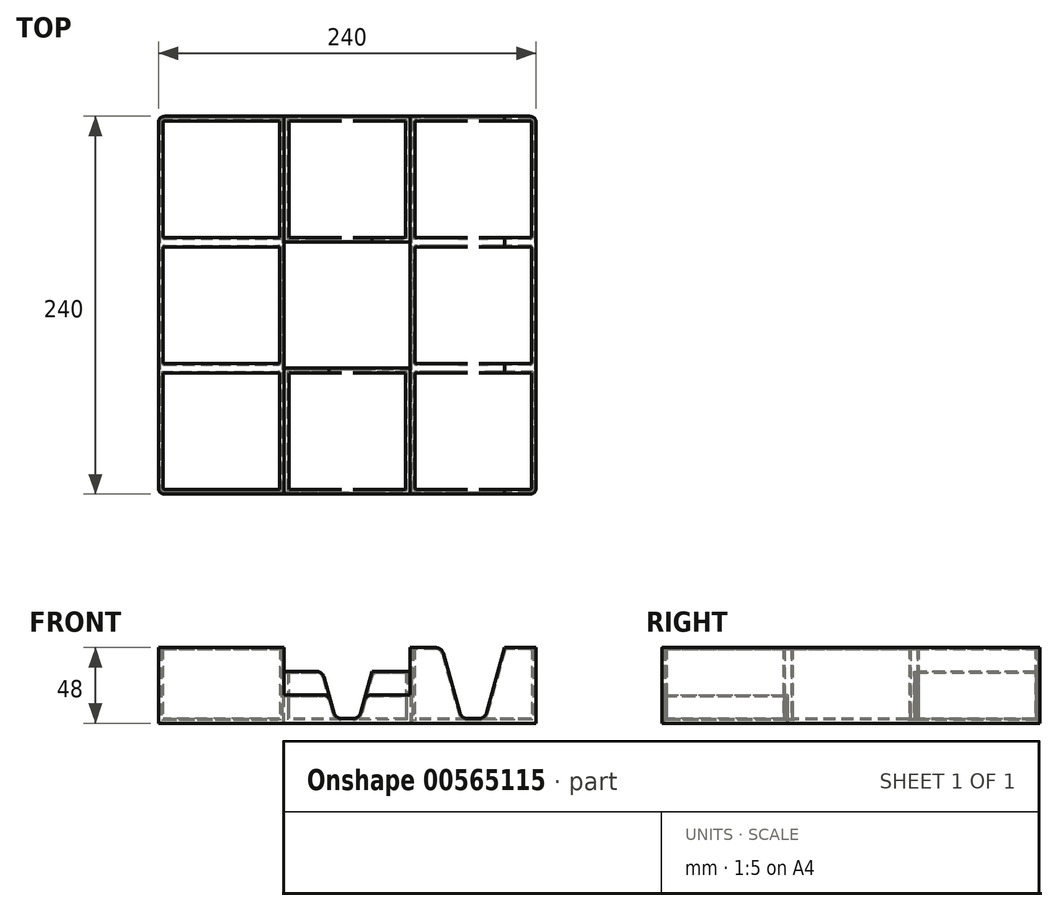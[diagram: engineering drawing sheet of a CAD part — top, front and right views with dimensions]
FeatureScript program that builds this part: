
annotation { "Feature Type Name" : "Feature", "Feature Type Description" : "" }
export const myFeature = defineFeature(function(context is Context, id is Id, definition is map)
    precondition{}
    {
        {
            var Q0;
            Q0=qCreatedBy(makeId("Top.planeOp"),FACE);
            var sketch = newSketch(context, id + "F0", { "sketchPlane" : qUnion([Q0])});
            skLineSegment(sketch, "E0.bottom", {"start": v(120, 120) * mm, "end": v(-120, 120) * mm});
            skLineSegment(sketch, "E0.top", {"start": v(120, -120) * mm, "end": v(-120, -120) * mm});
            skLineSegment(sketch, "E0.left", {"start": v(120, 120) * mm, "end": v(120, -120) * mm});
            skLineSegment(sketch, "E0.right", {"start": v(-120, 120) * mm, "end": v(-120, -120) * mm});
            skPoint(sketch, "E0.middle", {"position": v(0, 0) * mm});
            skSolve(sketch);
        }
        {
            var Q0;
            Q0 = qSketchRegion(id + "F0", true);
            extrude(context, id + "F1", {"entities" : qUnion([Q0]), "depth" : 3 * mm, "offsetDistance" : 25 * mm});
        }
        {
            var Q0;
            Q0=makeQuery(id+"F1.opExtrude","CAP_FACE",FACE,{"disambiguationData":[OSD([sQuery(id+"F0.wireOp",EDGE,"E0.bottom"),sQuery(id+"F0.wireOp",EDGE,"E0.top"),sQuery(id+"F0.wireOp",EDGE,"E0.left"),sQuery(id+"F0.wireOp",EDGE,"E0.right")])],"isStart":false});
            var sketch = newSketch(context, id + "F2", { "sketchPlane" : qUnion([Q0])});
            skLineSegment(sketch, "E1.bottom", {"start": v(117, 117) * mm, "end": v(-117, 117) * mm});
            skLineSegment(sketch, "E1.top", {"start": v(117, -117) * mm, "end": v(-117, -117) * mm});
            skLineSegment(sketch, "E1.left", {"start": v(117, 117) * mm, "end": v(117, -117) * mm});
            skLineSegment(sketch, "E1.right", {"start": v(-117, 117) * mm, "end": v(-117, -117) * mm});
            skPoint(sketch, "E1.middle", {"position": v(0, 0) * mm});
            skLineSegment(sketch, "E2.0", {"start": v(120, 120) * mm, "end": v(-120, 120) * mm});
            skLineSegment(sketch, "E3.0", {"start": v(-120, 120) * mm, "end": v(-120, -120) * mm});
            skLineSegment(sketch, "E4.0", {"start": v(120, 120) * mm, "end": v(120, -120) * mm});
            skLineSegment(sketch, "E5.0", {"start": v(120, -120) * mm, "end": v(-120, -120) * mm});
            skSolve(sketch);
        }
        {
            var Q0;
            Q0 = qSketchRegion(id + "F2", true);
            extrude(context, id + "F3", {"entities" : qUnion([Q0]), "operationType" : NewBodyOperationType.ADD, "depth" : 45 * mm, "offsetDistance" : 25 * mm});
        }
        {
            var Q0;
            Q0=makeQuery(id+"F1.opExtrude","CAP_FACE",FACE,{"disambiguationData":[OSD([sQuery(id+"F0.wireOp",EDGE,"E0.bottom"),sQuery(id+"F0.wireOp",EDGE,"E0.top"),sQuery(id+"F0.wireOp",EDGE,"E0.left"),sQuery(id+"F0.wireOp",EDGE,"E0.right")])],"isStart":false});
            var sketch = newSketch(context, id + "F4", { "sketchPlane" : qUnion([Q0])});
            skLineSegment(sketch, "E6.bottom", {"start": v(-40, -117) * mm, "end": v(-43, -117) * mm});
            skLineSegment(sketch, "E6.top", {"start": v(-40, 117) * mm, "end": v(-43, 117) * mm});
            skLineSegment(sketch, "E6.left", {"start": v(-40, -117) * mm, "end": v(-40, 117) * mm});
            skLineSegment(sketch, "E6.right", {"start": v(-43, -117) * mm, "end": v(-43, 117) * mm});
            skPoint(sketch, "E6.middle", {"position": v(-41.5, 0) * mm});
            skLineSegment(sketch, "E7.MirrorCS", {"start": v(40, 117) * mm, "end": v(43, 117) * mm});
            skLineSegment(sketch, "E8.MirrorCS", {"start": v(40, -117) * mm, "end": v(43, -117) * mm});
            skLineSegment(sketch, "E9.MirrorCS", {"start": v(40, -117) * mm, "end": v(40, 117) * mm});
            skLineSegment(sketch, "E10.MirrorCS", {"start": v(43, -117) * mm, "end": v(43, 117) * mm});
            skPoint(sketch, "E11.MirrorP", {"position": v(41.5, 0) * mm});
            skSolve(sketch);
        }
        {
            var Q0;
            Q0 = qSketchRegion(id + "F4", true);
            var Q1;
            Q1=makeQuery(id+"F3.opExtrude","CAP_FACE",FACE,{"disambiguationData":[OSD([sQuery(id+"F2.wireOp",EDGE,"E1.bottom"),sQuery(id+"F2.wireOp",EDGE,"E1.top"),sQuery(id+"F2.wireOp",EDGE,"E1.left"),sQuery(id+"F2.wireOp",EDGE,"E1.right"),sQuery(id+"F2.wireOp",EDGE,"E2.0"),sQuery(id+"F2.wireOp",EDGE,"E3.0"),sQuery(id+"F2.wireOp",EDGE,"E4.0"),sQuery(id+"F2.wireOp",EDGE,"E5.0")])],"isStart":false});
            extrude(context, id + "F5", {"entities" : qUnion([Q0]), "operationType" : NewBodyOperationType.ADD, "endBound" : BoundingType.UP_TO_SURFACE, "depth" : 25 * mm, "endBoundEntityFace" : qUnion([Q1]), "offsetDistance" : 25 * mm});
        }
        {
            var Q0;
            Q0=makeQuery(id+"F5.boolean.opBoolean","SPLIT",FACE,{"disambiguationData":[TD([makeQuery(id+"F3.opExtrude","SWEPT_FACE",FACE,{"disambiguationData":[OSD([sQuery(id+"F2.wireOp",EDGE,"E1.right")])]})])],"derivedFrom":makeQuery(id+"F1.opExtrude","CAP_FACE",FACE,{"disambiguationData":[OSD([sQuery(id+"F0.wireOp",EDGE,"E0.bottom"),sQuery(id+"F0.wireOp",EDGE,"E0.top"),sQuery(id+"F0.wireOp",EDGE,"E0.left"),sQuery(id+"F0.wireOp",EDGE,"E0.right")])],"isStart":false})});
            var sketch = newSketch(context, id + "F6", { "sketchPlane" : qUnion([Q0])});
            skLineSegment(sketch, "E12.bottom", {"start": v(-117, 37) * mm, "end": v(-43, 37) * mm});
            skLineSegment(sketch, "E12.top", {"start": v(-117, 43) * mm, "end": v(-43, 43) * mm});
            skLineSegment(sketch, "E12.left", {"start": v(-117, 37) * mm, "end": v(-117, 43) * mm});
            skLineSegment(sketch, "E12.right", {"start": v(-43, 37) * mm, "end": v(-43, 43) * mm});
            skLineSegment(sketch, "E13.MirrorCS", {"start": v(43, 37) * mm, "end": v(43, 43) * mm});
            skLineSegment(sketch, "E14.MirrorCS", {"start": v(117, 37) * mm, "end": v(117, 43) * mm});
            skLineSegment(sketch, "E15.MirrorCS", {"start": v(117, 43) * mm, "end": v(43, 43) * mm});
            skLineSegment(sketch, "E16.MirrorCS", {"start": v(117, 37) * mm, "end": v(43, 37) * mm});
            skLineSegment(sketch, "E17.MirrorCS", {"start": v(-43, -37) * mm, "end": v(-43, -43) * mm});
            skLineSegment(sketch, "E18.MirrorCS", {"start": v(-117, -37) * mm, "end": v(-117, -43) * mm});
            skLineSegment(sketch, "E19.MirrorCS", {"start": v(43, -37) * mm, "end": v(43, -43) * mm});
            skLineSegment(sketch, "E20.MirrorCS", {"start": v(117, -37) * mm, "end": v(117, -43) * mm});
            skLineSegment(sketch, "E21.MirrorCS", {"start": v(117, -37) * mm, "end": v(43, -37) * mm});
            skLineSegment(sketch, "E22.MirrorCS", {"start": v(-117, -43) * mm, "end": v(-43, -43) * mm});
            skLineSegment(sketch, "E23.MirrorCS", {"start": v(-117, -37) * mm, "end": v(-43, -37) * mm});
            skLineSegment(sketch, "E24.MirrorCS", {"start": v(117, -43) * mm, "end": v(43, -43) * mm});
            skSolve(sketch);
        }
        {
            var Q0;
            Q0 = qSketchRegion(id + "F6", true);
            var Q1;
            Q1=makeQuery(id+"F5.boolean.opBoolean","MERGE",FACE,{"derivedFrom":[makeQuery(id+"F3.opExtrude","CAP_FACE",FACE,{"disambiguationData":[OSD([sQuery(id+"F2.wireOp",EDGE,"E1.bottom"),sQuery(id+"F2.wireOp",EDGE,"E1.top"),sQuery(id+"F2.wireOp",EDGE,"E1.left"),sQuery(id+"F2.wireOp",EDGE,"E1.right"),sQuery(id+"F2.wireOp",EDGE,"E2.0"),sQuery(id+"F2.wireOp",EDGE,"E3.0"),sQuery(id+"F2.wireOp",EDGE,"E4.0"),sQuery(id+"F2.wireOp",EDGE,"E5.0")])],"isStart":false}),makeQuery(id+"F5.opExtrude","CAP_FACE",FACE,{"disambiguationData":[OSD([sQuery(id+"F4.wireOp",EDGE,"E6.bottom"),sQuery(id+"F4.wireOp",EDGE,"E6.top"),sQuery(id+"F4.wireOp",EDGE,"E6.left"),sQuery(id+"F4.wireOp",EDGE,"E6.right")])],"isStart":false}),makeQuery(id+"F5.opExtrude","CAP_FACE",FACE,{"disambiguationData":[OSD([sQuery(id+"F4.wireOp",EDGE,"E7.MirrorCS"),sQuery(id+"F4.wireOp",EDGE,"E8.MirrorCS"),sQuery(id+"F4.wireOp",EDGE,"E9.MirrorCS"),sQuery(id+"F4.wireOp",EDGE,"E10.MirrorCS")])],"isStart":false})]});
            extrude(context, id + "F7", {"entities" : qUnion([Q0]), "operationType" : NewBodyOperationType.ADD, "endBound" : BoundingType.UP_TO_SURFACE, "depth" : 25 * mm, "endBoundEntityFace" : qUnion([Q1]), "offsetDistance" : 25 * mm});
        }
        {
            var Q0;
            Q0=makeQuery(id+"F3.boolean.opBoolean","MERGE",FACE,{"derivedFrom":[makeQuery(id+"F1.opExtrude","SWEPT_FACE",FACE,{"disambiguationData":[OSD([sQuery(id+"F0.wireOp",EDGE,"E0.bottom")])]}),makeQuery(id+"F3.opExtrude","SWEPT_FACE",FACE,{"disambiguationData":[OSD([sQuery(id+"F2.wireOp",EDGE,"E2.0")])]})]});
            var sketch = newSketch(context, id + "F8", { "sketchPlane" : qUnion([Q0])});
            skLineSegment(sketch, "E25", {"start": v(-80, 48) * mm, "end": v(-80, 0) * mm, "construction": true});
            skLineSegment(sketch, "E26", {"start": v(-100, 48) * mm, "end": v(-60, 48) * mm});
            skLineSegment(sketch, "E27", {"start": v(-60, 48) * mm, "end": v(-72.5, 3) * mm});
            skLineSegment(sketch, "E28", {"start": v(-72.5, 3) * mm, "end": v(-87.5, 3) * mm});
            skLineSegment(sketch, "E29", {"start": v(-87.5, 3) * mm, "end": v(-100, 48) * mm});
            skSolve(sketch);
        }
        {
            var Q0;
            Q0 = qSketchRegion(id + "F8", true);
            extrude(context, id + "F9", {"entities" : qUnion([Q0]), "operationType" : NewBodyOperationType.REMOVE, "endBound" : BoundingType.THROUGH_ALL, "oppositeDirection" : true, "depth" : 25 * mm, "offsetDistance" : 25 * mm});
        }
        {
            var Q0;
            Q0=makeQuery(id+"F5.boolean.opBoolean","SPLIT",FACE,{"disambiguationData":[TD([makeQuery(id+"F5.opExtrude","SWEPT_FACE",FACE,{"disambiguationData":[OSD([sQuery(id+"F4.wireOp",EDGE,"E6.left")])]})])],"derivedFrom":makeQuery(id+"F1.opExtrude","CAP_FACE",FACE,{"disambiguationData":[OSD([sQuery(id+"F0.wireOp",EDGE,"E0.bottom"),sQuery(id+"F0.wireOp",EDGE,"E0.top"),sQuery(id+"F0.wireOp",EDGE,"E0.left"),sQuery(id+"F0.wireOp",EDGE,"E0.right")])],"isStart":false})});
            var sketch = newSketch(context, id + "F10", { "sketchPlane" : qUnion([Q0])});
            skLineSegment(sketch, "E30.bottom", {"start": v(-40, 43) * mm, "end": v(40, 43) * mm});
            skLineSegment(sketch, "E30.top", {"start": v(-40, 40) * mm, "end": v(40, 40) * mm});
            skLineSegment(sketch, "E30.left", {"start": v(-40, 43) * mm, "end": v(-40, 40) * mm});
            skLineSegment(sketch, "E30.right", {"start": v(40, 43) * mm, "end": v(40, 40) * mm});
            skSolve(sketch);
        }
        {
            var Q0;
            Q0 = qSketchRegion(id + "F10", true);
            extrude(context, id + "F11", {"entities" : qUnion([Q0]), "operationType" : NewBodyOperationType.ADD, "depth" : 30 * mm, "offsetDistance" : 25 * mm});
        }
        {
            var Q0;
            Q0=makeQuery(id+"F3.boolean.opBoolean","MERGE",FACE,{"derivedFrom":[makeQuery(id+"F1.opExtrude","SWEPT_FACE",FACE,{"disambiguationData":[OSD([sQuery(id+"F0.wireOp",EDGE,"E0.bottom")])]}),makeQuery(id+"F3.opExtrude","SWEPT_FACE",FACE,{"disambiguationData":[OSD([sQuery(id+"F2.wireOp",EDGE,"E2.0")])]})]});
            var sketch = newSketch(context, id + "F12", { "sketchPlane" : qUnion([Q0])});
            skLineSegment(sketch, "E31", {"start": v(-40, 48) * mm, "end": v(-40, 33) * mm});
            skLineSegment(sketch, "E32", {"start": v(-40, 33) * mm, "end": v(-15.83, 33) * mm});
            skLineSegment(sketch, "E33", {"start": v(-20, 48) * mm, "end": v(-15.83, 33) * mm, "construction": true});
            skLineSegment(sketch, "E34", {"start": v(-7.5, 3) * mm, "end": v(7.5, 3) * mm});
            skLineSegment(sketch, "E35", {"start": v(7.5, 3) * mm, "end": v(15.83, 33) * mm});
            skLineSegment(sketch, "E36", {"start": v(15.83, 33) * mm, "end": v(40, 33) * mm});
            skLineSegment(sketch, "E37", {"start": v(40, 33) * mm, "end": v(40, 48) * mm});
            skLineSegment(sketch, "E38", {"start": v(40, 48) * mm, "end": v(-40, 48) * mm});
            skLineSegment(sketch, "E39", {"start": v(-15.83, 33) * mm, "end": v(-7.5, 3) * mm});
            skLineSegment(sketch, "E40", {"start": v(15.83, 33) * mm, "end": v(20, 48) * mm, "construction": true});
            skSolve(sketch);
        }
        {
            var Q0;
            Q0 = qSketchRegion(id + "F12", true);
            var Q1;
            Q1=makeQuery(id+"F11.opExtrude","SWEPT_FACE",FACE,{"disambiguationData":[OSD([sQuery(id+"F10.wireOp",EDGE,"E30.top")])]});
            extrude(context, id + "F13", {"entities" : qUnion([Q0]), "operationType" : NewBodyOperationType.REMOVE, "endBound" : BoundingType.UP_TO_SURFACE, "oppositeDirection" : true, "depth" : 25 * mm, "endBoundEntityFace" : qUnion([Q1]), "offsetDistance" : 25 * mm});
        }
        {
            var Q0;
            {var subQ0=makeQuery(id+"F3.opExtrude","SWEPT_FACE",FACE,{"disambiguationData":[OSD([sQuery(id+"F2.wireOp",EDGE,"E1.top")])]});var subQ1=makeQuery(id+"F5.opExtrude","SWEPT_FACE",FACE,{"disambiguationData":[OSD([sQuery(id+"F4.wireOp",EDGE,"E6.left")])]});var subQ3=makeQuery(id+"F3.opExtrude","SWEPT_FACE",FACE,{"disambiguationData":[OSD([sQuery(id+"F2.wireOp",EDGE,"E1.bottom")])]});var subQ4=makeQuery(id+"F5.boolean.opBoolean","SPLIT",FACE,{"disambiguationData":[TD([subQ1])],"derivedFrom":makeQuery(id+"F1.opExtrude","CAP_FACE",FACE,{"disambiguationData":[OSD([sQuery(id+"F0.wireOp",EDGE,"E0.bottom"),sQuery(id+"F0.wireOp",EDGE,"E0.top"),sQuery(id+"F0.wireOp",EDGE,"E0.left"),sQuery(id+"F0.wireOp",EDGE,"E0.right")])],"isStart":false})});Q0=makeQuery(id+"F13.boolean.opBoolean","MERGE",FACE,{"derivedFrom":[makeQuery(id+"F11.boolean.opBoolean","SPLIT",FACE,{"disambiguationData":[TD([subQ3])],"derivedFrom":subQ4}),makeQuery(id+"F11.boolean.opBoolean","SPLIT",FACE,{"disambiguationData":[TD([subQ0])],"derivedFrom":subQ4})],"fromTools":[makeQuery(id+"F13.opExtrude","SWEPT_FACE",FACE,{"disambiguationData":[OSD([sQuery(id+"F12.wireOp",EDGE,"E34")])]})]});}
            var sketch = newSketch(context, id + "F14", { "sketchPlane" : qUnion([Q0])});
            skLineSegment(sketch, "E41.bottom", {"start": v(40, 43) * mm, "end": v(37, 43) * mm});
            skLineSegment(sketch, "E41.top", {"start": v(40, 117) * mm, "end": v(37, 117) * mm});
            skLineSegment(sketch, "E41.left", {"start": v(40, 43) * mm, "end": v(40, 117) * mm});
            skLineSegment(sketch, "E41.right", {"start": v(37, 43) * mm, "end": v(37, 117) * mm});
            skLineSegment(sketch, "E42.bottom", {"start": v(-37, 43) * mm, "end": v(-40, 43) * mm});
            skLineSegment(sketch, "E42.top", {"start": v(-37, 117) * mm, "end": v(-40, 117) * mm});
            skLineSegment(sketch, "E42.left", {"start": v(-37, 43) * mm, "end": v(-37, 117) * mm});
            skLineSegment(sketch, "E42.right", {"start": v(-40, 43) * mm, "end": v(-40, 117) * mm});
            skSolve(sketch);
        }
        {
            var Q0;
            Q0 = qSketchRegion(id + "F14", true);
            var Q1;
            Q1=makeQuery(id+"F13.boolean.opBoolean","COPY",FACE,{"derivedFrom":makeQuery(id+"F13.opExtrude","SWEPT_FACE",FACE,{"disambiguationData":[OSD([sQuery(id+"F12.wireOp",EDGE,"E32")])]})});
            extrude(context, id + "F15", {"entities" : qUnion([Q0]), "operationType" : NewBodyOperationType.ADD, "endBound" : BoundingType.UP_TO_SURFACE, "depth" : 25 * mm, "endBoundEntityFace" : qUnion([Q1]), "offsetDistance" : 25 * mm});
        }
        {
            var Q0;
            {var subQ0=makeQuery(id+"F3.opExtrude","SWEPT_FACE",FACE,{"disambiguationData":[OSD([sQuery(id+"F2.wireOp",EDGE,"E1.top")])]});var subQ1=makeQuery(id+"F5.opExtrude","SWEPT_FACE",FACE,{"disambiguationData":[OSD([sQuery(id+"F4.wireOp",EDGE,"E6.left")])]});var subQ3=makeQuery(id+"F3.opExtrude","SWEPT_FACE",FACE,{"disambiguationData":[OSD([sQuery(id+"F2.wireOp",EDGE,"E1.bottom")])]});var subQ4=makeQuery(id+"F5.boolean.opBoolean","SPLIT",FACE,{"disambiguationData":[TD([subQ1])],"derivedFrom":makeQuery(id+"F1.opExtrude","CAP_FACE",FACE,{"disambiguationData":[OSD([sQuery(id+"F0.wireOp",EDGE,"E0.bottom"),sQuery(id+"F0.wireOp",EDGE,"E0.top"),sQuery(id+"F0.wireOp",EDGE,"E0.left"),sQuery(id+"F0.wireOp",EDGE,"E0.right")])],"isStart":false})});Q0=makeQuery(id+"F13.boolean.opBoolean","MERGE",FACE,{"derivedFrom":[makeQuery(id+"F11.boolean.opBoolean","SPLIT",FACE,{"disambiguationData":[TD([subQ3])],"derivedFrom":subQ4}),makeQuery(id+"F11.boolean.opBoolean","SPLIT",FACE,{"disambiguationData":[TD([subQ0])],"derivedFrom":subQ4})],"fromTools":[makeQuery(id+"F13.opExtrude","SWEPT_FACE",FACE,{"disambiguationData":[OSD([sQuery(id+"F12.wireOp",EDGE,"E34")])]})]});}
            var sketch = newSketch(context, id + "F16", { "sketchPlane" : qUnion([Q0])});
            skLineSegment(sketch, "E43.bottom", {"start": v(40, -40) * mm, "end": v(-40, -40) * mm});
            skLineSegment(sketch, "E43.top", {"start": v(40, -43) * mm, "end": v(-40, -43) * mm});
            skLineSegment(sketch, "E43.left", {"start": v(40, -40) * mm, "end": v(40, -43) * mm});
            skLineSegment(sketch, "E43.right", {"start": v(-40, -40) * mm, "end": v(-40, -43) * mm});
            skSolve(sketch);
        }
        {
            var Q0;
            Q0 = qSketchRegion(id + "F16", true);
            extrude(context, id + "F17", {"entities" : qUnion([Q0]), "operationType" : NewBodyOperationType.ADD, "depth" : 15 * mm, "offsetDistance" : 25 * mm});
        }
        {
            var Q0;
            Q0=makeQuery(id+"F3.boolean.opBoolean","MERGE",FACE,{"derivedFrom":[makeQuery(id+"F1.opExtrude","SWEPT_FACE",FACE,{"disambiguationData":[OSD([sQuery(id+"F0.wireOp",EDGE,"E0.top")])]}),makeQuery(id+"F3.opExtrude","SWEPT_FACE",FACE,{"disambiguationData":[OSD([sQuery(id+"F2.wireOp",EDGE,"E5.0")])]})]});
            var sketch = newSketch(context, id + "F18", { "sketchPlane" : qUnion([Q0])});
            skLineSegment(sketch, "E44", {"start": v(-40, 48) * mm, "end": v(-40, 18) * mm});
            skLineSegment(sketch, "E45", {"start": v(-40, 18) * mm, "end": v(-11.67, 18) * mm});
            skLineSegment(sketch, "E46", {"start": v(-20, 48) * mm, "end": v(-11.67, 18) * mm, "construction": true});
            skLineSegment(sketch, "E47", {"start": v(-7.5, 3) * mm, "end": v(7.5, 3) * mm});
            skLineSegment(sketch, "E48", {"start": v(7.5, 3) * mm, "end": v(11.67, 18) * mm});
            skLineSegment(sketch, "E49", {"start": v(11.67, 18) * mm, "end": v(40, 18) * mm});
            skLineSegment(sketch, "E50", {"start": v(40, 18) * mm, "end": v(40, 48) * mm});
            skLineSegment(sketch, "E51", {"start": v(40, 48) * mm, "end": v(-40, 48) * mm});
            skLineSegment(sketch, "E52", {"start": v(-11.67, 18) * mm, "end": v(-7.5, 3) * mm});
            skLineSegment(sketch, "E53", {"start": v(11.67, 18) * mm, "end": v(20, 48) * mm, "construction": true});
            skSolve(sketch);
        }
        {
            var Q0;
            Q0 = qSketchRegion(id + "F18", true);
            var Q1;
            Q1=makeQuery(id+"F17.opExtrude","SWEPT_FACE",FACE,{"disambiguationData":[OSD([sQuery(id+"F16.wireOp",EDGE,"E43.bottom")])]});
            extrude(context, id + "F19", {"entities" : qUnion([Q0]), "operationType" : NewBodyOperationType.REMOVE, "endBound" : BoundingType.UP_TO_SURFACE, "oppositeDirection" : true, "depth" : 25 * mm, "endBoundEntityFace" : qUnion([Q1]), "offsetDistance" : 25 * mm});
        }
        {
            var Q0;
            {var subQ1=makeQuery(id+"F3.opExtrude","SWEPT_FACE",FACE,{"disambiguationData":[OSD([sQuery(id+"F2.wireOp",EDGE,"E1.bottom")])]});var subQ2=sQuery(id+"F0.wireOp",EDGE,"E0.bottom");var subQ3=makeQuery(id+"F1.opExtrude","CAP_FACE",FACE,{"disambiguationData":[OSD([subQ2,sQuery(id+"F0.wireOp",EDGE,"E0.top"),sQuery(id+"F0.wireOp",EDGE,"E0.left"),sQuery(id+"F0.wireOp",EDGE,"E0.right")])],"isStart":false});var subQ4=makeQuery(id+"F1.opExtrude","SWEPT_FACE",FACE,{"disambiguationData":[OSD([subQ2])]});var subQ5=makeQuery(id+"F13.opExtrude","SWEPT_FACE",FACE,{"disambiguationData":[OSD([sQuery(id+"F12.wireOp",EDGE,"E34")])]});var subQ9=makeQuery(id+"F5.opExtrude","SWEPT_FACE",FACE,{"disambiguationData":[OSD([sQuery(id+"F4.wireOp",EDGE,"E6.left")])]});var subQ15=makeQuery(id+"F3.opExtrude","SWEPT_FACE",FACE,{"disambiguationData":[OSD([sQuery(id+"F2.wireOp",EDGE,"E1.top")])]});var subQ16=makeQuery(id+"F5.boolean.opBoolean","SPLIT",FACE,{"disambiguationData":[TD([subQ9])],"derivedFrom":subQ3});var subQ17=makeQuery(id+"F13.boolean.opBoolean","MERGE",FACE,{"derivedFrom":[makeQuery(id+"F11.boolean.opBoolean","SPLIT",FACE,{"disambiguationData":[TD([subQ1])],"derivedFrom":subQ16}),makeQuery(id+"F11.boolean.opBoolean","SPLIT",FACE,{"disambiguationData":[TD([subQ15])],"derivedFrom":subQ16})],"fromTools":[subQ5]});Q0=makeQuery(id+"F19.boolean.opBoolean","MERGE",FACE,{"derivedFrom":[makeQuery(id+"F17.boolean.opBoolean","SPLIT",FACE,{"disambiguationData":[TD([subQ15])],"derivedFrom":subQ17}),makeQuery(id+"F17.boolean.opBoolean","SPLIT",FACE,{"disambiguationData":[TD([subQ4])],"derivedFrom":subQ17})],"fromTools":[makeQuery(id+"F19.opExtrude","SWEPT_FACE",FACE,{"disambiguationData":[OSD([sQuery(id+"F18.wireOp",EDGE,"E47")])]})]});}
            var sketch = newSketch(context, id + "F20", { "sketchPlane" : qUnion([Q0])});
            skLineSegment(sketch, "E54.bottom", {"start": v(-40, -117) * mm, "end": v(-37, -117) * mm});
            skLineSegment(sketch, "E54.top", {"start": v(-40, -43) * mm, "end": v(-37, -43) * mm});
            skLineSegment(sketch, "E54.left", {"start": v(-40, -117) * mm, "end": v(-40, -43) * mm});
            skLineSegment(sketch, "E54.right", {"start": v(-37, -117) * mm, "end": v(-37, -43) * mm});
            skLineSegment(sketch, "E55.bottom", {"start": v(40, -117) * mm, "end": v(37, -117) * mm});
            skLineSegment(sketch, "E55.top", {"start": v(40, -43) * mm, "end": v(37, -43) * mm});
            skLineSegment(sketch, "E55.left", {"start": v(40, -117) * mm, "end": v(40, -43) * mm});
            skLineSegment(sketch, "E55.right", {"start": v(37, -117) * mm, "end": v(37, -43) * mm});
            skSolve(sketch);
        }
        {
            var Q0;
            Q0 = qSketchRegion(id + "F20", true);
            var Q1;
            {var subQ0=sQuery(id+"F16.wireOp",EDGE,"E43.top");var subQ1=sQuery(id+"F16.wireOp",EDGE,"E43.bottom");Q1=makeQuery(id+"F19.boolean.opBoolean","SPLIT",FACE,{"disambiguationData":[TD([makeQuery(id+"F5.opExtrude","SWEPT_FACE",FACE,{"disambiguationData":[OSD([sQuery(id+"F4.wireOp",EDGE,"E6.left")])]})])],"derivedFrom":makeQuery(id+"F17.opExtrude","CAP_FACE",FACE,{"disambiguationData":[OSD([subQ1,subQ0,sQuery(id+"F16.wireOp",EDGE,"E43.left"),sQuery(id+"F16.wireOp",EDGE,"E43.right")])],"isStart":false})});}
            extrude(context, id + "F21", {"entities" : qUnion([Q0]), "operationType" : NewBodyOperationType.ADD, "endBound" : BoundingType.UP_TO_SURFACE, "depth" : 25 * mm, "endBoundEntityFace" : qUnion([Q1]), "offsetDistance" : 25 * mm});
        }
        {
            var Q0;
            {var subQ1=makeQuery(id+"F3.opExtrude","SWEPT_FACE",FACE,{"disambiguationData":[OSD([sQuery(id+"F2.wireOp",EDGE,"E1.bottom")])]});var subQ2=sQuery(id+"F0.wireOp",EDGE,"E0.bottom");var subQ3=makeQuery(id+"F1.opExtrude","CAP_FACE",FACE,{"disambiguationData":[OSD([subQ2,sQuery(id+"F0.wireOp",EDGE,"E0.top"),sQuery(id+"F0.wireOp",EDGE,"E0.left"),sQuery(id+"F0.wireOp",EDGE,"E0.right")])],"isStart":false});var subQ4=makeQuery(id+"F1.opExtrude","SWEPT_FACE",FACE,{"disambiguationData":[OSD([subQ2])]});var subQ5=makeQuery(id+"F13.opExtrude","SWEPT_FACE",FACE,{"disambiguationData":[OSD([sQuery(id+"F12.wireOp",EDGE,"E34")])]});var subQ9=makeQuery(id+"F5.opExtrude","SWEPT_FACE",FACE,{"disambiguationData":[OSD([sQuery(id+"F4.wireOp",EDGE,"E6.left")])]});var subQ15=makeQuery(id+"F3.opExtrude","SWEPT_FACE",FACE,{"disambiguationData":[OSD([sQuery(id+"F2.wireOp",EDGE,"E1.top")])]});var subQ16=makeQuery(id+"F5.boolean.opBoolean","SPLIT",FACE,{"disambiguationData":[TD([subQ9])],"derivedFrom":subQ3});var subQ17=makeQuery(id+"F13.boolean.opBoolean","MERGE",FACE,{"derivedFrom":[makeQuery(id+"F11.boolean.opBoolean","SPLIT",FACE,{"disambiguationData":[TD([subQ1])],"derivedFrom":subQ16}),makeQuery(id+"F11.boolean.opBoolean","SPLIT",FACE,{"disambiguationData":[TD([subQ15])],"derivedFrom":subQ16})],"fromTools":[subQ5]});Q0=makeQuery(id+"F19.boolean.opBoolean","MERGE",FACE,{"derivedFrom":[makeQuery(id+"F17.boolean.opBoolean","SPLIT",FACE,{"disambiguationData":[TD([subQ15])],"derivedFrom":subQ17}),makeQuery(id+"F17.boolean.opBoolean","SPLIT",FACE,{"disambiguationData":[TD([subQ4])],"derivedFrom":subQ17})],"fromTools":[makeQuery(id+"F19.opExtrude","SWEPT_FACE",FACE,{"disambiguationData":[OSD([sQuery(id+"F18.wireOp",EDGE,"E47")])]})]});}
            var sketch = newSketch(context, id + "F22", { "sketchPlane" : qUnion([Q0])});
            skLineSegment(sketch, "E56.bottom", {"start": v(40, -40) * mm, "end": v(-40, -40) * mm});
            skLineSegment(sketch, "E56.top", {"start": v(40, 40) * mm, "end": v(-40, 40) * mm});
            skLineSegment(sketch, "E56.left", {"start": v(40, -40) * mm, "end": v(40, 40) * mm});
            skLineSegment(sketch, "E56.right", {"start": v(-40, -40) * mm, "end": v(-40, 40) * mm});
            skSolve(sketch);
        }
        {
            var Q0;
            Q0 = qSketchRegion(id + "F22", true);
            extrude(context, id + "F23", {"entities" : qUnion([Q0]), "operationType" : NewBodyOperationType.REMOVE, "endBound" : BoundingType.THROUGH_ALL, "oppositeDirection" : true, "depth" : 25 * mm, "offsetDistance" : 25 * mm});
        }
        {
            var Q0;
            {var subQ3=sQuery(id+"F2.wireOp",EDGE,"E2.0");var subQ8=sQuery(id+"F8.wireOp",EDGE,"E29");Q0=makeQuery(id+"F9.boolean.opBoolean","COPY",EDGE,{"disambiguationData":[TD([makeQuery(id+"F1.opExtrude","SWEPT_FACE",FACE,{"disambiguationData":[OSD([sQuery(id+"F0.wireOp",EDGE,"E0.bottom")])]})])],"derivedFrom":makeQuery(id+"F9.opExtrude","SWEPT_EDGE",EDGE,{"disambiguationData":[OSD([subQ3,sQuery(id+"F8.wireOp",EDGE,"E26"),subQ8])]})});}
            var Q1;
            {var subQ3=sQuery(id+"F2.wireOp",EDGE,"E2.0");var subQ8=sQuery(id+"F8.wireOp",EDGE,"E27");Q1=makeQuery(id+"F9.boolean.opBoolean","COPY",EDGE,{"disambiguationData":[TD([makeQuery(id+"F1.opExtrude","SWEPT_FACE",FACE,{"disambiguationData":[OSD([sQuery(id+"F0.wireOp",EDGE,"E0.bottom")])]})])],"derivedFrom":makeQuery(id+"F9.opExtrude","SWEPT_EDGE",EDGE,{"disambiguationData":[OSD([subQ3,sQuery(id+"F8.wireOp",EDGE,"E26"),subQ8])]})});}
            var Q2;
            {var subQ0=sQuery(id+"F0.wireOp",EDGE,"E0.bottom");var subQ1=sQuery(id+"F8.wireOp",EDGE,"E28");var subQ2=sQuery(id+"F8.wireOp",EDGE,"E29");Q2=makeQuery(id+"F9.boolean.opBoolean","COPY",EDGE,{"disambiguationData":[TD([makeQuery(id+"F1.opExtrude","SWEPT_FACE",FACE,{"disambiguationData":[OSD([subQ0])]})])],"derivedFrom":makeQuery(id+"F9.opExtrude","SWEPT_EDGE",EDGE,{"disambiguationData":[OSD([subQ1,subQ2])]})});}
            var Q3;
            {var subQ0=sQuery(id+"F0.wireOp",EDGE,"E0.bottom");var subQ1=sQuery(id+"F8.wireOp",EDGE,"E27");var subQ2=sQuery(id+"F8.wireOp",EDGE,"E28");Q3=makeQuery(id+"F9.boolean.opBoolean","COPY",EDGE,{"disambiguationData":[TD([makeQuery(id+"F1.opExtrude","SWEPT_FACE",FACE,{"disambiguationData":[OSD([subQ0])]})])],"derivedFrom":makeQuery(id+"F9.opExtrude","SWEPT_EDGE",EDGE,{"disambiguationData":[OSD([subQ1,subQ2])]})});}
            var Q4;
            {var subQ0=sQuery(id+"F8.wireOp",EDGE,"E27");var subQ1=sQuery(id+"F8.wireOp",EDGE,"E28");Q4=makeQuery(id+"F9.boolean.opBoolean","COPY",EDGE,{"disambiguationData":[TD([makeQuery(id+"F7.opExtrude","SWEPT_FACE",FACE,{"disambiguationData":[OSD([sQuery(id+"F6.wireOp",EDGE,"E15.MirrorCS")])]})])],"derivedFrom":makeQuery(id+"F9.opExtrude","SWEPT_EDGE",EDGE,{"disambiguationData":[OSD([subQ0,subQ1])]})});}
            var Q5;
            {var subQ1=sQuery(id+"F6.wireOp",EDGE,"E15.MirrorCS");var subQ2=sQuery(id+"F8.wireOp",EDGE,"E27");var subQ3=sQuery(id+"F2.wireOp",EDGE,"E2.0");Q5=makeQuery(id+"F9.boolean.opBoolean","COPY",EDGE,{"disambiguationData":[TD([makeQuery(id+"F7.opExtrude","SWEPT_FACE",FACE,{"disambiguationData":[OSD([subQ1])]})])],"derivedFrom":makeQuery(id+"F9.opExtrude","SWEPT_EDGE",EDGE,{"disambiguationData":[OSD([subQ3,sQuery(id+"F8.wireOp",EDGE,"E26"),subQ2])]})});}
            var Q6;
            {var subQ1=sQuery(id+"F6.wireOp",EDGE,"E15.MirrorCS");var subQ2=sQuery(id+"F2.wireOp",EDGE,"E2.0");var subQ3=sQuery(id+"F8.wireOp",EDGE,"E29");Q6=makeQuery(id+"F9.boolean.opBoolean","COPY",EDGE,{"disambiguationData":[TD([makeQuery(id+"F7.opExtrude","SWEPT_FACE",FACE,{"disambiguationData":[OSD([subQ1])]})])],"derivedFrom":makeQuery(id+"F9.opExtrude","SWEPT_EDGE",EDGE,{"disambiguationData":[OSD([subQ2,sQuery(id+"F8.wireOp",EDGE,"E26"),subQ3])]})});}
            var Q7;
            {var subQ0=sQuery(id+"F8.wireOp",EDGE,"E28");var subQ1=sQuery(id+"F8.wireOp",EDGE,"E29");Q7=makeQuery(id+"F9.boolean.opBoolean","COPY",EDGE,{"disambiguationData":[TD([makeQuery(id+"F7.opExtrude","SWEPT_FACE",FACE,{"disambiguationData":[OSD([sQuery(id+"F6.wireOp",EDGE,"E15.MirrorCS")])]})])],"derivedFrom":makeQuery(id+"F9.opExtrude","SWEPT_EDGE",EDGE,{"disambiguationData":[OSD([subQ0,subQ1])]})});}
            var Q8;
            {var subQ0=sQuery(id+"F8.wireOp",EDGE,"E28");var subQ1=sQuery(id+"F8.wireOp",EDGE,"E29");Q8=makeQuery(id+"F9.boolean.opBoolean","COPY",EDGE,{"disambiguationData":[TD([makeQuery(id+"F7.opExtrude","SWEPT_FACE",FACE,{"disambiguationData":[OSD([sQuery(id+"F6.wireOp",EDGE,"E21.MirrorCS")])]})])],"derivedFrom":makeQuery(id+"F9.opExtrude","SWEPT_EDGE",EDGE,{"disambiguationData":[OSD([subQ0,subQ1])]})});}
            var Q9;
            {var subQ0=sQuery(id+"F2.wireOp",EDGE,"E2.0");var subQ2=sQuery(id+"F6.wireOp",EDGE,"E21.MirrorCS");var subQ3=sQuery(id+"F8.wireOp",EDGE,"E29");Q9=makeQuery(id+"F9.boolean.opBoolean","COPY",EDGE,{"disambiguationData":[TD([makeQuery(id+"F7.opExtrude","SWEPT_FACE",FACE,{"disambiguationData":[OSD([subQ2])]})])],"derivedFrom":makeQuery(id+"F9.opExtrude","SWEPT_EDGE",EDGE,{"disambiguationData":[OSD([subQ0,sQuery(id+"F8.wireOp",EDGE,"E26"),subQ3])]})});}
            var Q10;
            {var subQ0=sQuery(id+"F8.wireOp",EDGE,"E27");var subQ1=sQuery(id+"F2.wireOp",EDGE,"E2.0");var subQ3=sQuery(id+"F6.wireOp",EDGE,"E21.MirrorCS");Q10=makeQuery(id+"F9.boolean.opBoolean","COPY",EDGE,{"disambiguationData":[TD([makeQuery(id+"F7.opExtrude","SWEPT_FACE",FACE,{"disambiguationData":[OSD([subQ3])]})])],"derivedFrom":makeQuery(id+"F9.opExtrude","SWEPT_EDGE",EDGE,{"disambiguationData":[OSD([subQ1,sQuery(id+"F8.wireOp",EDGE,"E26"),subQ0])]})});}
            var Q11;
            {var subQ0=sQuery(id+"F8.wireOp",EDGE,"E27");var subQ1=sQuery(id+"F8.wireOp",EDGE,"E28");Q11=makeQuery(id+"F9.boolean.opBoolean","COPY",EDGE,{"disambiguationData":[TD([makeQuery(id+"F7.opExtrude","SWEPT_FACE",FACE,{"disambiguationData":[OSD([sQuery(id+"F6.wireOp",EDGE,"E21.MirrorCS")])]})])],"derivedFrom":makeQuery(id+"F9.opExtrude","SWEPT_EDGE",EDGE,{"disambiguationData":[OSD([subQ0,subQ1])]})});}
            var Q12;
            {var subQ0=sQuery(id+"F0.wireOp",EDGE,"E0.top");var subQ1=sQuery(id+"F8.wireOp",EDGE,"E29");var subQ2=sQuery(id+"F8.wireOp",EDGE,"E28");Q12=makeQuery(id+"F9.boolean.opBoolean","COPY",EDGE,{"disambiguationData":[TD([makeQuery(id+"F1.opExtrude","SWEPT_FACE",FACE,{"disambiguationData":[OSD([subQ0])]})])],"derivedFrom":makeQuery(id+"F9.opExtrude","SWEPT_EDGE",EDGE,{"disambiguationData":[OSD([subQ2,subQ1])]})});}
            var Q13;
            {var subQ3=sQuery(id+"F2.wireOp",EDGE,"E2.0");var subQ8=sQuery(id+"F8.wireOp",EDGE,"E29");Q13=makeQuery(id+"F9.boolean.opBoolean","COPY",EDGE,{"disambiguationData":[TD([makeQuery(id+"F1.opExtrude","SWEPT_FACE",FACE,{"disambiguationData":[OSD([sQuery(id+"F0.wireOp",EDGE,"E0.top")])]})])],"derivedFrom":makeQuery(id+"F9.opExtrude","SWEPT_EDGE",EDGE,{"disambiguationData":[OSD([subQ3,sQuery(id+"F8.wireOp",EDGE,"E26"),subQ8])]})});}
            var Q14;
            {var subQ0=sQuery(id+"F0.wireOp",EDGE,"E0.top");var subQ1=sQuery(id+"F8.wireOp",EDGE,"E27");var subQ2=sQuery(id+"F8.wireOp",EDGE,"E28");Q14=makeQuery(id+"F9.boolean.opBoolean","COPY",EDGE,{"disambiguationData":[TD([makeQuery(id+"F1.opExtrude","SWEPT_FACE",FACE,{"disambiguationData":[OSD([subQ0])]})])],"derivedFrom":makeQuery(id+"F9.opExtrude","SWEPT_EDGE",EDGE,{"disambiguationData":[OSD([subQ1,subQ2])]})});}
            var Q15;
            {var subQ3=sQuery(id+"F2.wireOp",EDGE,"E2.0");var subQ8=sQuery(id+"F8.wireOp",EDGE,"E27");Q15=makeQuery(id+"F9.boolean.opBoolean","COPY",EDGE,{"disambiguationData":[TD([makeQuery(id+"F1.opExtrude","SWEPT_FACE",FACE,{"disambiguationData":[OSD([sQuery(id+"F0.wireOp",EDGE,"E0.top")])]})])],"derivedFrom":makeQuery(id+"F9.opExtrude","SWEPT_EDGE",EDGE,{"disambiguationData":[OSD([subQ3,sQuery(id+"F8.wireOp",EDGE,"E26"),subQ8])]})});}
            var Q16;
            {var subQ0=sQuery(id+"F0.wireOp",EDGE,"E0.bottom");var subQ1=sQuery(id+"F12.wireOp",EDGE,"E34");var subQ2=sQuery(id+"F12.wireOp",EDGE,"E35");Q16=makeQuery(id+"F13.boolean.opBoolean","COPY",EDGE,{"disambiguationData":[TD([makeQuery(id+"F1.opExtrude","SWEPT_FACE",FACE,{"disambiguationData":[OSD([subQ0])]})])],"derivedFrom":makeQuery(id+"F13.opExtrude","SWEPT_EDGE",EDGE,{"disambiguationData":[OSD([subQ1,subQ2])]})});}
            var Q17;
            {var subQ0=sQuery(id+"F12.wireOp",EDGE,"E35");var subQ1=sQuery(id+"F12.wireOp",EDGE,"E36");Q17=makeQuery(id+"F13.boolean.opBoolean","COPY",EDGE,{"disambiguationData":[topologyDisambiguationEdgeConnected([makeQuery(id+"F13.opExtrude","SWEPT_FACE",FACE,{"disambiguationData":[OSD([subQ1])]})])],"derivedFrom":makeQuery(id+"F13.opExtrude","SWEPT_EDGE",EDGE,{"disambiguationData":[OSD([subQ0,subQ1])]})});}
            var Q18;
            {var subQ0=sQuery(id+"F12.wireOp",EDGE,"E32");var subQ1=sQuery(id+"F12.wireOp",EDGE,"E39");Q18=makeQuery(id+"F13.boolean.opBoolean","COPY",EDGE,{"disambiguationData":[topologyDisambiguationEdgeConnected([makeQuery(id+"F13.opExtrude","SWEPT_FACE",FACE,{"disambiguationData":[OSD([subQ0])]})])],"derivedFrom":makeQuery(id+"F13.opExtrude","SWEPT_EDGE",EDGE,{"disambiguationData":[OSD([subQ0,subQ1])]})});}
            var Q19;
            {var subQ0=sQuery(id+"F0.wireOp",EDGE,"E0.bottom");var subQ1=sQuery(id+"F12.wireOp",EDGE,"E34");var subQ2=sQuery(id+"F12.wireOp",EDGE,"E39");Q19=makeQuery(id+"F13.boolean.opBoolean","COPY",EDGE,{"disambiguationData":[TD([makeQuery(id+"F1.opExtrude","SWEPT_FACE",FACE,{"disambiguationData":[OSD([subQ0])]})])],"derivedFrom":makeQuery(id+"F13.opExtrude","SWEPT_EDGE",EDGE,{"disambiguationData":[OSD([subQ1,subQ2])]})});}
            var Q20;
            {var subQ0=sQuery(id+"F12.wireOp",EDGE,"E34");var subQ1=sQuery(id+"F12.wireOp",EDGE,"E39");Q20=makeQuery(id+"F13.boolean.opBoolean","COPY",EDGE,{"disambiguationData":[TD([makeQuery(id+"F11.opExtrude","SWEPT_FACE",FACE,{"disambiguationData":[OSD([sQuery(id+"F10.wireOp",EDGE,"E30.bottom")])]})])],"derivedFrom":makeQuery(id+"F13.opExtrude","SWEPT_EDGE",EDGE,{"disambiguationData":[OSD([subQ0,subQ1])]})});}
            var Q21;
            {var subQ0=sQuery(id+"F12.wireOp",EDGE,"E35");Q21=makeQuery(id+"F13.boolean.opBoolean","COPY",EDGE,{"disambiguationData":[topologyDisambiguationEdgeConnected([makeQuery(id+"F11.opExtrude","CAP_FACE",FACE,{"disambiguationData":[OSD([sQuery(id+"F10.wireOp",EDGE,"E30.bottom"),sQuery(id+"F10.wireOp",EDGE,"E30.top"),sQuery(id+"F10.wireOp",EDGE,"E30.left"),sQuery(id+"F10.wireOp",EDGE,"E30.right")])],"isStart":false})])],"derivedFrom":makeQuery(id+"F13.opExtrude","SWEPT_EDGE",EDGE,{"disambiguationData":[OSD([subQ0,sQuery(id+"F12.wireOp",EDGE,"E36")])]})});}
            var Q22;
            {var subQ0=sQuery(id+"F12.wireOp",EDGE,"E39");Q22=makeQuery(id+"F13.boolean.opBoolean","COPY",EDGE,{"disambiguationData":[topologyDisambiguationEdgeConnected([makeQuery(id+"F11.opExtrude","CAP_FACE",FACE,{"disambiguationData":[OSD([sQuery(id+"F10.wireOp",EDGE,"E30.bottom"),sQuery(id+"F10.wireOp",EDGE,"E30.top"),sQuery(id+"F10.wireOp",EDGE,"E30.left"),sQuery(id+"F10.wireOp",EDGE,"E30.right")])],"isStart":false})])],"derivedFrom":makeQuery(id+"F13.opExtrude","SWEPT_EDGE",EDGE,{"disambiguationData":[OSD([sQuery(id+"F12.wireOp",EDGE,"E32"),subQ0])]})});}
            var Q23;
            {var subQ0=sQuery(id+"F12.wireOp",EDGE,"E34");var subQ1=sQuery(id+"F12.wireOp",EDGE,"E35");Q23=makeQuery(id+"F13.boolean.opBoolean","COPY",EDGE,{"disambiguationData":[TD([makeQuery(id+"F11.opExtrude","SWEPT_FACE",FACE,{"disambiguationData":[OSD([sQuery(id+"F10.wireOp",EDGE,"E30.bottom")])]})])],"derivedFrom":makeQuery(id+"F13.opExtrude","SWEPT_EDGE",EDGE,{"disambiguationData":[OSD([subQ0,subQ1])]})});}
            var Q24;
            {var subQ0=sQuery(id+"F18.wireOp",EDGE,"E47");var subQ1=sQuery(id+"F18.wireOp",EDGE,"E52");Q24=makeQuery(id+"F19.boolean.opBoolean","COPY",EDGE,{"disambiguationData":[TD([makeQuery(id+"F17.opExtrude","SWEPT_FACE",FACE,{"disambiguationData":[OSD([sQuery(id+"F16.wireOp",EDGE,"E43.bottom")])]})])],"derivedFrom":makeQuery(id+"F19.opExtrude","SWEPT_EDGE",EDGE,{"disambiguationData":[OSD([subQ0,subQ1])]})});}
            var Q25;
            {var subQ0=sQuery(id+"F18.wireOp",EDGE,"E52");Q25=makeQuery(id+"F19.boolean.opBoolean","COPY",EDGE,{"disambiguationData":[topologyDisambiguationEdgeConnected([makeQuery(id+"F17.opExtrude","CAP_FACE",FACE,{"disambiguationData":[OSD([sQuery(id+"F16.wireOp",EDGE,"E43.bottom"),sQuery(id+"F16.wireOp",EDGE,"E43.top"),sQuery(id+"F16.wireOp",EDGE,"E43.left"),sQuery(id+"F16.wireOp",EDGE,"E43.right")])],"isStart":false})])],"derivedFrom":makeQuery(id+"F19.opExtrude","SWEPT_EDGE",EDGE,{"disambiguationData":[OSD([sQuery(id+"F18.wireOp",EDGE,"E45"),subQ0])]})});}
            var Q26;
            {var subQ0=sQuery(id+"F18.wireOp",EDGE,"E48");Q26=makeQuery(id+"F19.boolean.opBoolean","COPY",EDGE,{"disambiguationData":[topologyDisambiguationEdgeConnected([makeQuery(id+"F17.opExtrude","CAP_FACE",FACE,{"disambiguationData":[OSD([sQuery(id+"F16.wireOp",EDGE,"E43.bottom"),sQuery(id+"F16.wireOp",EDGE,"E43.top"),sQuery(id+"F16.wireOp",EDGE,"E43.left"),sQuery(id+"F16.wireOp",EDGE,"E43.right")])],"isStart":false})])],"derivedFrom":makeQuery(id+"F19.opExtrude","SWEPT_EDGE",EDGE,{"disambiguationData":[OSD([subQ0,sQuery(id+"F18.wireOp",EDGE,"E49")])]})});}
            var Q27;
            {var subQ0=sQuery(id+"F18.wireOp",EDGE,"E47");var subQ1=sQuery(id+"F18.wireOp",EDGE,"E48");Q27=makeQuery(id+"F19.boolean.opBoolean","COPY",EDGE,{"disambiguationData":[TD([makeQuery(id+"F17.opExtrude","SWEPT_FACE",FACE,{"disambiguationData":[OSD([sQuery(id+"F16.wireOp",EDGE,"E43.bottom")])]})])],"derivedFrom":makeQuery(id+"F19.opExtrude","SWEPT_EDGE",EDGE,{"disambiguationData":[OSD([subQ0,subQ1])]})});}
            var Q28;
            {var subQ0=sQuery(id+"F18.wireOp",EDGE,"E48");var subQ1=sQuery(id+"F18.wireOp",EDGE,"E49");Q28=makeQuery(id+"F19.boolean.opBoolean","COPY",EDGE,{"disambiguationData":[topologyDisambiguationEdgeConnected([makeQuery(id+"F19.opExtrude","SWEPT_FACE",FACE,{"disambiguationData":[OSD([subQ1])]})])],"derivedFrom":makeQuery(id+"F19.opExtrude","SWEPT_EDGE",EDGE,{"disambiguationData":[OSD([subQ0,subQ1])]})});}
            var Q29;
            {var subQ0=sQuery(id+"F0.wireOp",EDGE,"E0.top");var subQ1=sQuery(id+"F18.wireOp",EDGE,"E47");var subQ2=sQuery(id+"F18.wireOp",EDGE,"E48");Q29=makeQuery(id+"F19.boolean.opBoolean","COPY",EDGE,{"disambiguationData":[TD([makeQuery(id+"F1.opExtrude","SWEPT_FACE",FACE,{"disambiguationData":[OSD([subQ0])]})])],"derivedFrom":makeQuery(id+"F19.opExtrude","SWEPT_EDGE",EDGE,{"disambiguationData":[OSD([subQ1,subQ2])]})});}
            var Q30;
            {var subQ0=sQuery(id+"F18.wireOp",EDGE,"E45");var subQ1=sQuery(id+"F18.wireOp",EDGE,"E52");Q30=makeQuery(id+"F19.boolean.opBoolean","COPY",EDGE,{"disambiguationData":[topologyDisambiguationEdgeConnected([makeQuery(id+"F19.opExtrude","SWEPT_FACE",FACE,{"disambiguationData":[OSD([subQ0])]})])],"derivedFrom":makeQuery(id+"F19.opExtrude","SWEPT_EDGE",EDGE,{"disambiguationData":[OSD([subQ0,subQ1])]})});}
            var Q31;
            {var subQ0=sQuery(id+"F0.wireOp",EDGE,"E0.top");var subQ1=sQuery(id+"F18.wireOp",EDGE,"E47");var subQ2=sQuery(id+"F18.wireOp",EDGE,"E52");Q31=makeQuery(id+"F19.boolean.opBoolean","COPY",EDGE,{"disambiguationData":[TD([makeQuery(id+"F1.opExtrude","SWEPT_FACE",FACE,{"disambiguationData":[OSD([subQ0])]})])],"derivedFrom":makeQuery(id+"F19.opExtrude","SWEPT_EDGE",EDGE,{"disambiguationData":[OSD([subQ1,subQ2])]})});}
            var Q32;
            {var subQ3=sQuery(id+"F2.wireOp",EDGE,"E2.0");var subQ8=sQuery(id+"F8.wireOp",EDGE,"E27");Q32=makeQuery(id+"FlesIIsrEHbjO6k_1.1.F9.boolean.opBoolean","COPY",EDGE,{"disambiguationData":[TD([makeQuery(id+"F1.opExtrude","SWEPT_FACE",FACE,{"disambiguationData":[OSD([sQuery(id+"F0.wireOp",EDGE,"E0.bottom")])]})])],"derivedFrom":makeQuery(id+"FlesIIsrEHbjO6k_1.1.F9.opExtrude","SWEPT_EDGE",EDGE,{"disambiguationData":[OSD([subQ3,sQuery(id+"F8.wireOp",EDGE,"E26"),subQ8])]})});}
            var Q33;
            {var subQ0=sQuery(id+"F0.wireOp",EDGE,"E0.bottom");var subQ1=sQuery(id+"F8.wireOp",EDGE,"E27");var subQ2=sQuery(id+"F8.wireOp",EDGE,"E28");Q33=makeQuery(id+"FlesIIsrEHbjO6k_1.1.F9.boolean.opBoolean","COPY",EDGE,{"disambiguationData":[TD([makeQuery(id+"F1.opExtrude","SWEPT_FACE",FACE,{"disambiguationData":[OSD([subQ0])]})])],"derivedFrom":makeQuery(id+"FlesIIsrEHbjO6k_1.1.F9.opExtrude","SWEPT_EDGE",EDGE,{"disambiguationData":[OSD([subQ1,subQ2])]})});}
            var Q34;
            {var subQ3=sQuery(id+"F2.wireOp",EDGE,"E2.0");var subQ8=sQuery(id+"F8.wireOp",EDGE,"E29");Q34=makeQuery(id+"FlesIIsrEHbjO6k_1.1.F9.boolean.opBoolean","COPY",EDGE,{"disambiguationData":[TD([makeQuery(id+"F1.opExtrude","SWEPT_FACE",FACE,{"disambiguationData":[OSD([sQuery(id+"F0.wireOp",EDGE,"E0.bottom")])]})])],"derivedFrom":makeQuery(id+"FlesIIsrEHbjO6k_1.1.F9.opExtrude","SWEPT_EDGE",EDGE,{"disambiguationData":[OSD([subQ3,sQuery(id+"F8.wireOp",EDGE,"E26"),subQ8])]})});}
            var Q35;
            {var subQ0=sQuery(id+"F8.wireOp",EDGE,"E27");var subQ1=sQuery(id+"F8.wireOp",EDGE,"E28");Q35=makeQuery(id+"FlesIIsrEHbjO6k_1.1.F9.boolean.opBoolean","COPY",EDGE,{"disambiguationData":[TD([makeQuery(id+"F7.opExtrude","SWEPT_FACE",FACE,{"disambiguationData":[OSD([sQuery(id+"F6.wireOp",EDGE,"E12.bottom")])]})])],"derivedFrom":makeQuery(id+"FlesIIsrEHbjO6k_1.1.F9.opExtrude","SWEPT_EDGE",EDGE,{"disambiguationData":[OSD([subQ0,subQ1])]})});}
            var Q36;
            {var subQ0=sQuery(id+"F6.wireOp",EDGE,"E12.bottom");var subQ1=sQuery(id+"F2.wireOp",EDGE,"E2.0");var subQ3=sQuery(id+"F8.wireOp",EDGE,"E27");Q36=makeQuery(id+"FlesIIsrEHbjO6k_1.1.F9.boolean.opBoolean","COPY",EDGE,{"disambiguationData":[TD([makeQuery(id+"F7.opExtrude","SWEPT_FACE",FACE,{"disambiguationData":[OSD([subQ0])]})])],"derivedFrom":makeQuery(id+"FlesIIsrEHbjO6k_1.1.F9.opExtrude","SWEPT_EDGE",EDGE,{"disambiguationData":[OSD([subQ1,sQuery(id+"F8.wireOp",EDGE,"E26"),subQ3])]})});}
            var Q37;
            {var subQ0=sQuery(id+"F6.wireOp",EDGE,"E12.bottom");var subQ1=sQuery(id+"F2.wireOp",EDGE,"E2.0");var subQ3=sQuery(id+"F8.wireOp",EDGE,"E29");Q37=makeQuery(id+"FlesIIsrEHbjO6k_1.1.F9.boolean.opBoolean","COPY",EDGE,{"disambiguationData":[TD([makeQuery(id+"F7.opExtrude","SWEPT_FACE",FACE,{"disambiguationData":[OSD([subQ0])]})])],"derivedFrom":makeQuery(id+"FlesIIsrEHbjO6k_1.1.F9.opExtrude","SWEPT_EDGE",EDGE,{"disambiguationData":[OSD([subQ1,sQuery(id+"F8.wireOp",EDGE,"E26"),subQ3])]})});}
            var Q38;
            {var subQ0=sQuery(id+"F8.wireOp",EDGE,"E28");var subQ1=sQuery(id+"F8.wireOp",EDGE,"E29");Q38=makeQuery(id+"FlesIIsrEHbjO6k_1.1.F9.boolean.opBoolean","COPY",EDGE,{"disambiguationData":[TD([makeQuery(id+"F7.opExtrude","SWEPT_FACE",FACE,{"disambiguationData":[OSD([sQuery(id+"F6.wireOp",EDGE,"E12.bottom")])]})])],"derivedFrom":makeQuery(id+"FlesIIsrEHbjO6k_1.1.F9.opExtrude","SWEPT_EDGE",EDGE,{"disambiguationData":[OSD([subQ0,subQ1])]})});}
            var Q39;
            {var subQ0=sQuery(id+"F8.wireOp",EDGE,"E29");var subQ1=sQuery(id+"F0.wireOp",EDGE,"E0.bottom");var subQ2=sQuery(id+"F8.wireOp",EDGE,"E28");Q39=makeQuery(id+"FlesIIsrEHbjO6k_1.1.F9.boolean.opBoolean","COPY",EDGE,{"disambiguationData":[TD([makeQuery(id+"F1.opExtrude","SWEPT_FACE",FACE,{"disambiguationData":[OSD([subQ1])]})])],"derivedFrom":makeQuery(id+"FlesIIsrEHbjO6k_1.1.F9.opExtrude","SWEPT_EDGE",EDGE,{"disambiguationData":[OSD([subQ2,subQ0])]})});}
            var Q40;
            {var subQ0=sQuery(id+"F8.wireOp",EDGE,"E28");var subQ1=sQuery(id+"F8.wireOp",EDGE,"E29");Q40=makeQuery(id+"FlesIIsrEHbjO6k_1.1.F9.boolean.opBoolean","COPY",EDGE,{"disambiguationData":[TD([makeQuery(id+"F7.opExtrude","SWEPT_FACE",FACE,{"disambiguationData":[OSD([sQuery(id+"F6.wireOp",EDGE,"E22.MirrorCS")])]})])],"derivedFrom":makeQuery(id+"FlesIIsrEHbjO6k_1.1.F9.opExtrude","SWEPT_EDGE",EDGE,{"disambiguationData":[OSD([subQ0,subQ1])]})});}
            var Q41;
            {var subQ0=sQuery(id+"F2.wireOp",EDGE,"E2.0");var subQ2=sQuery(id+"F6.wireOp",EDGE,"E22.MirrorCS");var subQ3=sQuery(id+"F8.wireOp",EDGE,"E29");Q41=makeQuery(id+"FlesIIsrEHbjO6k_1.1.F9.boolean.opBoolean","COPY",EDGE,{"disambiguationData":[TD([makeQuery(id+"F7.opExtrude","SWEPT_FACE",FACE,{"disambiguationData":[OSD([subQ2])]})])],"derivedFrom":makeQuery(id+"FlesIIsrEHbjO6k_1.1.F9.opExtrude","SWEPT_EDGE",EDGE,{"disambiguationData":[OSD([subQ0,sQuery(id+"F8.wireOp",EDGE,"E26"),subQ3])]})});}
            var Q42;
            {var subQ0=sQuery(id+"F2.wireOp",EDGE,"E2.0");var subQ2=sQuery(id+"F6.wireOp",EDGE,"E22.MirrorCS");var subQ3=sQuery(id+"F8.wireOp",EDGE,"E27");Q42=makeQuery(id+"FlesIIsrEHbjO6k_1.1.F9.boolean.opBoolean","COPY",EDGE,{"disambiguationData":[TD([makeQuery(id+"F7.opExtrude","SWEPT_FACE",FACE,{"disambiguationData":[OSD([subQ2])]})])],"derivedFrom":makeQuery(id+"FlesIIsrEHbjO6k_1.1.F9.opExtrude","SWEPT_EDGE",EDGE,{"disambiguationData":[OSD([subQ0,sQuery(id+"F8.wireOp",EDGE,"E26"),subQ3])]})});}
            var Q43;
            {var subQ0=sQuery(id+"F8.wireOp",EDGE,"E27");var subQ1=sQuery(id+"F8.wireOp",EDGE,"E28");Q43=makeQuery(id+"FlesIIsrEHbjO6k_1.1.F9.boolean.opBoolean","COPY",EDGE,{"disambiguationData":[TD([makeQuery(id+"F7.opExtrude","SWEPT_FACE",FACE,{"disambiguationData":[OSD([sQuery(id+"F6.wireOp",EDGE,"E22.MirrorCS")])]})])],"derivedFrom":makeQuery(id+"FlesIIsrEHbjO6k_1.1.F9.opExtrude","SWEPT_EDGE",EDGE,{"disambiguationData":[OSD([subQ0,subQ1])]})});}
            var Q44;
            {var subQ0=sQuery(id+"F0.wireOp",EDGE,"E0.top");var subQ1=sQuery(id+"F8.wireOp",EDGE,"E27");var subQ2=sQuery(id+"F8.wireOp",EDGE,"E28");Q44=makeQuery(id+"FlesIIsrEHbjO6k_1.1.F9.boolean.opBoolean","COPY",EDGE,{"disambiguationData":[TD([makeQuery(id+"F1.opExtrude","SWEPT_FACE",FACE,{"disambiguationData":[OSD([subQ0])]})])],"derivedFrom":makeQuery(id+"FlesIIsrEHbjO6k_1.1.F9.opExtrude","SWEPT_EDGE",EDGE,{"disambiguationData":[OSD([subQ1,subQ2])]})});}
            var Q45;
            {var subQ3=sQuery(id+"F2.wireOp",EDGE,"E2.0");var subQ8=sQuery(id+"F8.wireOp",EDGE,"E27");Q45=makeQuery(id+"FlesIIsrEHbjO6k_1.1.F9.boolean.opBoolean","COPY",EDGE,{"disambiguationData":[TD([makeQuery(id+"F1.opExtrude","SWEPT_FACE",FACE,{"disambiguationData":[OSD([sQuery(id+"F0.wireOp",EDGE,"E0.top")])]})])],"derivedFrom":makeQuery(id+"FlesIIsrEHbjO6k_1.1.F9.opExtrude","SWEPT_EDGE",EDGE,{"disambiguationData":[OSD([subQ3,sQuery(id+"F8.wireOp",EDGE,"E26"),subQ8])]})});}
            var Q46;
            {var subQ3=sQuery(id+"F2.wireOp",EDGE,"E2.0");var subQ8=sQuery(id+"F8.wireOp",EDGE,"E29");Q46=makeQuery(id+"FlesIIsrEHbjO6k_1.1.F9.boolean.opBoolean","COPY",EDGE,{"disambiguationData":[TD([makeQuery(id+"F1.opExtrude","SWEPT_FACE",FACE,{"disambiguationData":[OSD([sQuery(id+"F0.wireOp",EDGE,"E0.top")])]})])],"derivedFrom":makeQuery(id+"FlesIIsrEHbjO6k_1.1.F9.opExtrude","SWEPT_EDGE",EDGE,{"disambiguationData":[OSD([subQ3,sQuery(id+"F8.wireOp",EDGE,"E26"),subQ8])]})});}
            var Q47;
            {var subQ0=sQuery(id+"F0.wireOp",EDGE,"E0.top");var subQ1=sQuery(id+"F8.wireOp",EDGE,"E28");var subQ2=sQuery(id+"F8.wireOp",EDGE,"E29");Q47=makeQuery(id+"FlesIIsrEHbjO6k_1.1.F9.boolean.opBoolean","COPY",EDGE,{"disambiguationData":[TD([makeQuery(id+"F1.opExtrude","SWEPT_FACE",FACE,{"disambiguationData":[OSD([subQ0])]})])],"derivedFrom":makeQuery(id+"FlesIIsrEHbjO6k_1.1.F9.opExtrude","SWEPT_EDGE",EDGE,{"disambiguationData":[OSD([subQ1,subQ2])]})});}
            fillet(context, id + "F24", {"entities" : qUnion([Q0, Q1, Q2, Q3, Q4, Q5, Q6, Q7, Q8, Q9, Q10, Q11, Q12, Q13, Q14, Q15, Q16, Q17, Q18, Q19, Q20, Q21, Q22, Q23, Q24, Q25, Q26, Q27, Q28, Q29, Q30, Q31, Q32, Q33, Q34, Q35, Q36, Q37, Q38, Q39, Q40, Q41, Q42, Q43, Q44, Q45, Q46, Q47]), "radius" : 5 * mm, "tangentPropagation" : true, "allowEdgeOverflow" : false});
        }
        {
            var Q0;
            Q0=makeQuery(id+"F3.boolean.opBoolean","MERGE",EDGE,{"derivedFrom":[makeQuery(id+"F1.opExtrude","SWEPT_EDGE",EDGE,{"disambiguationData":[OSD([sQuery(id+"F0.wireOp",EDGE,"E0.bottom"),sQuery(id+"F0.wireOp",EDGE,"E0.left")])]}),makeQuery(id+"F3.opExtrude","SWEPT_EDGE",EDGE,{"disambiguationData":[OSD([sQuery(id+"F2.wireOp",EDGE,"E2.0"),sQuery(id+"F2.wireOp",EDGE,"E4.0")])]})]});
            var Q1;
            Q1=makeQuery(id+"F3.boolean.opBoolean","MERGE",EDGE,{"derivedFrom":[makeQuery(id+"F1.opExtrude","SWEPT_EDGE",EDGE,{"disambiguationData":[OSD([sQuery(id+"F0.wireOp",EDGE,"E0.bottom"),sQuery(id+"F0.wireOp",EDGE,"E0.right")])]}),makeQuery(id+"F3.opExtrude","SWEPT_EDGE",EDGE,{"disambiguationData":[OSD([sQuery(id+"F2.wireOp",EDGE,"E2.0"),sQuery(id+"F2.wireOp",EDGE,"E3.0")])]})]});
            var Q2;
            Q2=makeQuery(id+"F3.boolean.opBoolean","MERGE",EDGE,{"derivedFrom":[makeQuery(id+"F1.opExtrude","SWEPT_EDGE",EDGE,{"disambiguationData":[OSD([sQuery(id+"F0.wireOp",EDGE,"E0.top"),sQuery(id+"F0.wireOp",EDGE,"E0.right")])]}),makeQuery(id+"F3.opExtrude","SWEPT_EDGE",EDGE,{"disambiguationData":[OSD([sQuery(id+"F2.wireOp",EDGE,"E3.0"),sQuery(id+"F2.wireOp",EDGE,"E5.0")])]})]});
            var Q3;
            Q3=makeQuery(id+"F3.boolean.opBoolean","MERGE",EDGE,{"derivedFrom":[makeQuery(id+"F1.opExtrude","SWEPT_EDGE",EDGE,{"disambiguationData":[OSD([sQuery(id+"F0.wireOp",EDGE,"E0.top"),sQuery(id+"F0.wireOp",EDGE,"E0.left")])]}),makeQuery(id+"F3.opExtrude","SWEPT_EDGE",EDGE,{"disambiguationData":[OSD([sQuery(id+"F2.wireOp",EDGE,"E4.0"),sQuery(id+"F2.wireOp",EDGE,"E5.0")])]})]});
            var Q4;
            Q4=makeQuery(id+"F19.boolean.opBoolean","COPY",EDGE,{"derivedFrom":makeQuery(id+"F19.opExtrude","CAP_EDGE",EDGE,{"disambiguationData":[OSD([sQuery(id+"F18.wireOp",EDGE,"E50")])],"isStart":true})});
            var Q5;
            Q5=makeQuery(id+"F13.boolean.opBoolean","COPY",EDGE,{"derivedFrom":makeQuery(id+"F13.opExtrude","CAP_EDGE",EDGE,{"disambiguationData":[OSD([sQuery(id+"F12.wireOp",EDGE,"E31")])],"isStart":true})});
            var Q6;
            Q6=makeQuery(id+"F13.boolean.opBoolean","COPY",EDGE,{"derivedFrom":makeQuery(id+"F13.opExtrude","CAP_EDGE",EDGE,{"disambiguationData":[OSD([sQuery(id+"F12.wireOp",EDGE,"E37")])],"isStart":true})});
            var Q7;
            Q7=makeQuery(id+"F19.boolean.opBoolean","COPY",EDGE,{"derivedFrom":makeQuery(id+"F19.opExtrude","CAP_EDGE",EDGE,{"disambiguationData":[OSD([sQuery(id+"F18.wireOp",EDGE,"E44")])],"isStart":true})});
            fillet(context, id + "F25", {"entities" : qUnion([Q0, Q1, Q2, Q3, Q4, Q5, Q6, Q7]), "radius" : 4 * mm, "tangentPropagation" : true, "allowEdgeOverflow" : false});
        }
        {
            var Q0;
            Q0=makeQuery(id+"F7.opExtrude","SWEPT_EDGE",EDGE,{"disambiguationData":[OSD([sQuery(id+"F6.wireOp",EDGE,"E14.MirrorCS"),sQuery(id+"F6.wireOp",EDGE,"E15.MirrorCS")])]});
            var Q1;
            Q1=makeQuery(id+"F7.opExtrude","SWEPT_EDGE",EDGE,{"disambiguationData":[OSD([sQuery(id+"F6.wireOp",EDGE,"E20.MirrorCS"),sQuery(id+"F6.wireOp",EDGE,"E21.MirrorCS")])]});
            var Q2;
            Q2=makeQuery(id+"F3.opExtrude","SWEPT_EDGE",EDGE,{"disambiguationData":[OSD([sQuery(id+"F2.wireOp",EDGE,"E1.top"),sQuery(id+"F2.wireOp",EDGE,"E1.left")])]});
            var Q3;
            Q3=makeQuery(id+"F21.opExtrude","SWEPT_EDGE",EDGE,{"disambiguationData":[OSD([sQuery(id+"F2.wireOp",EDGE,"E1.top"),sQuery(id+"F20.wireOp",EDGE,"E55.bottom"),sQuery(id+"F20.wireOp",EDGE,"E55.right")])]});
            var Q4;
            Q4=makeQuery(id+"F15.opExtrude","SWEPT_EDGE",EDGE,{"disambiguationData":[OSD([sQuery(id+"F10.wireOp",EDGE,"E30.bottom"),sQuery(id+"F14.wireOp",EDGE,"E41.bottom"),sQuery(id+"F14.wireOp",EDGE,"E41.right")])]});
            var Q5;
            Q5=makeQuery(id+"F5.opExtrude","SWEPT_EDGE",EDGE,{"disambiguationData":[OSD([sQuery(id+"F2.wireOp",EDGE,"E1.top"),sQuery(id+"F4.wireOp",EDGE,"E6.bottom"),sQuery(id+"F4.wireOp",EDGE,"E6.right")])]});
            var Q6;
            Q6=makeQuery(id+"F7.opExtrude","SWEPT_EDGE",EDGE,{"disambiguationData":[OSD([sQuery(id+"F4.wireOp",EDGE,"E6.right"),sQuery(id+"F6.wireOp",EDGE,"E17.MirrorCS"),sQuery(id+"F6.wireOp",EDGE,"E23.MirrorCS")])]});
            var Q7;
            Q7=makeQuery(id+"F7.opExtrude","SWEPT_EDGE",EDGE,{"disambiguationData":[OSD([sQuery(id+"F4.wireOp",EDGE,"E6.right"),sQuery(id+"F6.wireOp",EDGE,"E12.top"),sQuery(id+"F6.wireOp",EDGE,"E12.right")])]});
            var Q8;
            Q8=makeQuery(id+"F5.opExtrude","SWEPT_EDGE",EDGE,{"disambiguationData":[OSD([sQuery(id+"F2.wireOp",EDGE,"E1.top"),sQuery(id+"F4.wireOp",EDGE,"E8.MirrorCS"),sQuery(id+"F4.wireOp",EDGE,"E10.MirrorCS")])]});
            var Q9;
            Q9=makeQuery(id+"F7.opExtrude","SWEPT_EDGE",EDGE,{"disambiguationData":[OSD([sQuery(id+"F6.wireOp",EDGE,"E19.MirrorCS"),sQuery(id+"F6.wireOp",EDGE,"E21.MirrorCS")])]});
            var Q10;
            Q10=makeQuery(id+"F7.opExtrude","SWEPT_EDGE",EDGE,{"disambiguationData":[OSD([sQuery(id+"F6.wireOp",EDGE,"E13.MirrorCS"),sQuery(id+"F6.wireOp",EDGE,"E15.MirrorCS")])]});
            var Q11;
            Q11=makeQuery(id+"F21.opExtrude","SWEPT_EDGE",EDGE,{"disambiguationData":[OSD([sQuery(id+"F2.wireOp",EDGE,"E1.top"),sQuery(id+"F20.wireOp",EDGE,"E54.bottom"),sQuery(id+"F20.wireOp",EDGE,"E54.right")])]});
            var Q12;
            Q12=makeQuery(id+"F15.opExtrude","SWEPT_EDGE",EDGE,{"disambiguationData":[OSD([sQuery(id+"F10.wireOp",EDGE,"E30.bottom"),sQuery(id+"F14.wireOp",EDGE,"E42.bottom"),sQuery(id+"F14.wireOp",EDGE,"E42.left")])]});
            var Q13;
            Q13=makeQuery(id+"F3.opExtrude","SWEPT_EDGE",EDGE,{"disambiguationData":[OSD([sQuery(id+"F2.wireOp",EDGE,"E1.top"),sQuery(id+"F2.wireOp",EDGE,"E1.right")])]});
            var Q14;
            Q14=makeQuery(id+"F7.opExtrude","SWEPT_EDGE",EDGE,{"disambiguationData":[OSD([sQuery(id+"F2.wireOp",EDGE,"E1.right"),sQuery(id+"F6.wireOp",EDGE,"E18.MirrorCS"),sQuery(id+"F6.wireOp",EDGE,"E23.MirrorCS")])]});
            var Q15;
            Q15=makeQuery(id+"F7.opExtrude","SWEPT_EDGE",EDGE,{"disambiguationData":[OSD([sQuery(id+"F2.wireOp",EDGE,"E1.right"),sQuery(id+"F6.wireOp",EDGE,"E12.top"),sQuery(id+"F6.wireOp",EDGE,"E12.left")])]});
            var Q16;
            Q16=makeQuery(id+"F3.opExtrude","SWEPT_EDGE",EDGE,{"disambiguationData":[OSD([sQuery(id+"F2.wireOp",EDGE,"E1.bottom"),sQuery(id+"F2.wireOp",EDGE,"E1.left")])]});
            var Q17;
            Q17=makeQuery(id+"F7.opExtrude","SWEPT_EDGE",EDGE,{"disambiguationData":[OSD([sQuery(id+"F6.wireOp",EDGE,"E14.MirrorCS"),sQuery(id+"F6.wireOp",EDGE,"E16.MirrorCS")])]});
            var Q18;
            Q18=makeQuery(id+"F7.opExtrude","SWEPT_EDGE",EDGE,{"disambiguationData":[OSD([sQuery(id+"F6.wireOp",EDGE,"E20.MirrorCS"),sQuery(id+"F6.wireOp",EDGE,"E24.MirrorCS")])]});
            var Q19;
            Q19=makeQuery(id+"F15.opExtrude","SWEPT_EDGE",EDGE,{"disambiguationData":[OSD([sQuery(id+"F2.wireOp",EDGE,"E1.bottom"),sQuery(id+"F14.wireOp",EDGE,"E41.top"),sQuery(id+"F14.wireOp",EDGE,"E41.right")])]});
            var Q20;
            Q20=makeQuery(id+"F21.opExtrude","SWEPT_EDGE",EDGE,{"disambiguationData":[OSD([sQuery(id+"F16.wireOp",EDGE,"E43.top"),sQuery(id+"F20.wireOp",EDGE,"E55.top"),sQuery(id+"F20.wireOp",EDGE,"E55.right")])]});
            var Q21;
            Q21=makeQuery(id+"F5.opExtrude","SWEPT_EDGE",EDGE,{"disambiguationData":[OSD([sQuery(id+"F2.wireOp",EDGE,"E1.bottom"),sQuery(id+"F4.wireOp",EDGE,"E6.top"),sQuery(id+"F4.wireOp",EDGE,"E6.right")])]});
            var Q22;
            Q22=makeQuery(id+"F7.opExtrude","SWEPT_EDGE",EDGE,{"disambiguationData":[OSD([sQuery(id+"F4.wireOp",EDGE,"E6.right"),sQuery(id+"F6.wireOp",EDGE,"E12.bottom"),sQuery(id+"F6.wireOp",EDGE,"E12.right")])]});
            var Q23;
            Q23=makeQuery(id+"F7.opExtrude","SWEPT_EDGE",EDGE,{"disambiguationData":[OSD([sQuery(id+"F4.wireOp",EDGE,"E6.right"),sQuery(id+"F6.wireOp",EDGE,"E17.MirrorCS"),sQuery(id+"F6.wireOp",EDGE,"E22.MirrorCS")])]});
            var Q24;
            Q24=makeQuery(id+"F7.opExtrude","SWEPT_EDGE",EDGE,{"disambiguationData":[OSD([sQuery(id+"F2.wireOp",EDGE,"E1.right"),sQuery(id+"F6.wireOp",EDGE,"E18.MirrorCS"),sQuery(id+"F6.wireOp",EDGE,"E22.MirrorCS")])]});
            var Q25;
            Q25=makeQuery(id+"F7.opExtrude","SWEPT_EDGE",EDGE,{"disambiguationData":[OSD([sQuery(id+"F2.wireOp",EDGE,"E1.right"),sQuery(id+"F6.wireOp",EDGE,"E12.bottom"),sQuery(id+"F6.wireOp",EDGE,"E12.left")])]});
            var Q26;
            Q26=makeQuery(id+"F3.opExtrude","SWEPT_EDGE",EDGE,{"disambiguationData":[OSD([sQuery(id+"F2.wireOp",EDGE,"E1.bottom"),sQuery(id+"F2.wireOp",EDGE,"E1.right")])]});
            var Q27;
            Q27=makeQuery(id+"F21.opExtrude","SWEPT_EDGE",EDGE,{"disambiguationData":[OSD([sQuery(id+"F16.wireOp",EDGE,"E43.top"),sQuery(id+"F20.wireOp",EDGE,"E54.top"),sQuery(id+"F20.wireOp",EDGE,"E54.right")])]});
            var Q28;
            Q28=makeQuery(id+"F15.opExtrude","SWEPT_EDGE",EDGE,{"disambiguationData":[OSD([sQuery(id+"F2.wireOp",EDGE,"E1.bottom"),sQuery(id+"F14.wireOp",EDGE,"E42.top"),sQuery(id+"F14.wireOp",EDGE,"E42.left")])]});
            var Q29;
            Q29=makeQuery(id+"F7.opExtrude","SWEPT_EDGE",EDGE,{"disambiguationData":[OSD([sQuery(id+"F6.wireOp",EDGE,"E19.MirrorCS"),sQuery(id+"F6.wireOp",EDGE,"E24.MirrorCS")])]});
            var Q30;
            Q30=makeQuery(id+"F7.opExtrude","SWEPT_EDGE",EDGE,{"disambiguationData":[OSD([sQuery(id+"F6.wireOp",EDGE,"E13.MirrorCS"),sQuery(id+"F6.wireOp",EDGE,"E16.MirrorCS")])]});
            var Q31;
            Q31=makeQuery(id+"F5.opExtrude","SWEPT_EDGE",EDGE,{"disambiguationData":[OSD([sQuery(id+"F2.wireOp",EDGE,"E1.bottom"),sQuery(id+"F4.wireOp",EDGE,"E7.MirrorCS"),sQuery(id+"F4.wireOp",EDGE,"E10.MirrorCS")])]});
            fillet(context, id + "F26", {"entities" : qUnion([Q0, Q1, Q2, Q3, Q4, Q5, Q6, Q7, Q8, Q9, Q10, Q11, Q12, Q13, Q14, Q15, Q16, Q17, Q18, Q19, Q20, Q21, Q22, Q23, Q24, Q25, Q26, Q27, Q28, Q29, Q30, Q31]), "radius" : 1 * mm, "tangentPropagation" : true, "allowEdgeOverflow" : false});
        }
        {
            var Q0;
            Q0=makeQuery(id+"F1.opExtrude","CAP_FACE",FACE,{"disambiguationData":[OSD([sQuery(id+"F0.wireOp",EDGE,"E0.bottom"),sQuery(id+"F0.wireOp",EDGE,"E0.top"),sQuery(id+"F0.wireOp",EDGE,"E0.left"),sQuery(id+"F0.wireOp",EDGE,"E0.right")])],"isStart":true});
            shell(context, id + "F27", {"entities" : qUnion([Q0]), "thickness" : 1 * mm});
        }
    });
